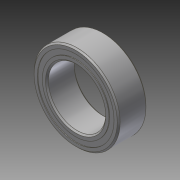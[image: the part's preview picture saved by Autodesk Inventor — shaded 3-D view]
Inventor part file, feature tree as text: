
AUTODESK INVENTOR PART (.ipt)
format: ipt  version: 2014 SP1 (Build 180222100, 222)  size: 586,240 bytes
history: native  units: in
note: dims shown in document units (in); Inventor stores cm internally (conversion verified against a paired STEP export)
features: imported_body x16, other x12, revolve x5
ambient origin geometry x8: Origin, YZ Plane, XZ Plane, XY Plane, X Axis, Y Axis, Z Axis, Center Point
bodies: Body1 (feature_tree), Body2 (feature_tree), Body3 (feature_tree), Body4 (feature_tree), Body5 (feature_tree), Body6 (feature_tree), Body7 (feature_tree), Body8 (feature_tree), Body9 (feature_tree), Body10 (feature_tree), Body11 (feature_tree), Body12 (feature_tree), Body13 (feature_tree), Body14 (feature_tree), Body15 (feature_tree), Body16 (feature_tree)
feature tree (33):
  revolve  "Revolve1"  [1 undecoded]
  other  "217-2788_57155K375.ipt1"
  revolve  "Revolve3"  [1 undecoded]
  revolve  "Revolve4"  [1 undecoded]
  other  "CirPattern1[1]"
  other  "CirPattern1[2]"
  other  "CirPattern1[3]"
  other  "CirPattern1[4]"
  other  "CirPattern1[5]"
  other  "CirPattern1[6]"
  other  "CirPattern1[7]"
  other  "CirPattern1[8]"
  other  "CirPattern1[9]"
  other  "CirPattern1[10]"
  other  "CirPattern1[11]"
  revolve  "Revolve5[1]"  [1 undecoded]
  revolve  "Revolve5[2]"  [1 undecoded]
  imported_body  "Base1"
  imported_body  "Base2"
  imported_body  "Base3"
  imported_body  "Base4"
  imported_body  "Base5"
  imported_body  "Base6"
  imported_body  "Base7"
  imported_body  "Base8"
  imported_body  "Base9"
  imported_body  "Base10"
  imported_body  "Base11"
  imported_body  "Base12"
  imported_body  "Base13"
  imported_body  "Base14"
  imported_body  "Base15"
  imported_body  "Base16"
note: 5 required parameter values undecoded (feature->parameter linkage not recoverable at this tier; creation-order binding heuristic only, values carry confidence <= 0.55)
